# Revit family: Planet-Wattohm Colonnes Logix Kit Ovaline
name_source: partatom
category: Installations électriques
units: mm (PartAtom-declared; Revit-internal decimal feet)

## family parameters
Conserver l'orientation des annotations = Non
Cote de connecteur circulaire = Utiliser le diamètre
Couper avec des vides une fois chargée = Non
Hôte = Face
Partagée = Non
Point de calcul de pièce = Non
Type d'élément = Normal

## types (2) — shared parameters
Fabricant = PLANET WATTOHM
Finition = Aluminium
Matériau principal = Aluminium
Nombre de compartiments = Autre
Standard = Ovaline
h1 = 2700 mm  [stored 8.85827 ft]
zero-valued in all types: Elévation par défaut

## per-type parameters (varying)
| type | Description | Modèle |
| kit Ovaline Colonnette 1 cpt Alu | Tablette support en corian Blanc pour Colonnettes LOGIX équipé d'un chargeur induction | PW-32360 |
| kit Ovaline Colonnette 2 cpt Alu | Kit extension Ovaline. Vient se fixer sur une Colonnette 1 compartiment | PW-32361 |

note: [stored X ft] marks values corroborated as IEEE doubles in the binary element streams (Revit-internal decimal feet)
